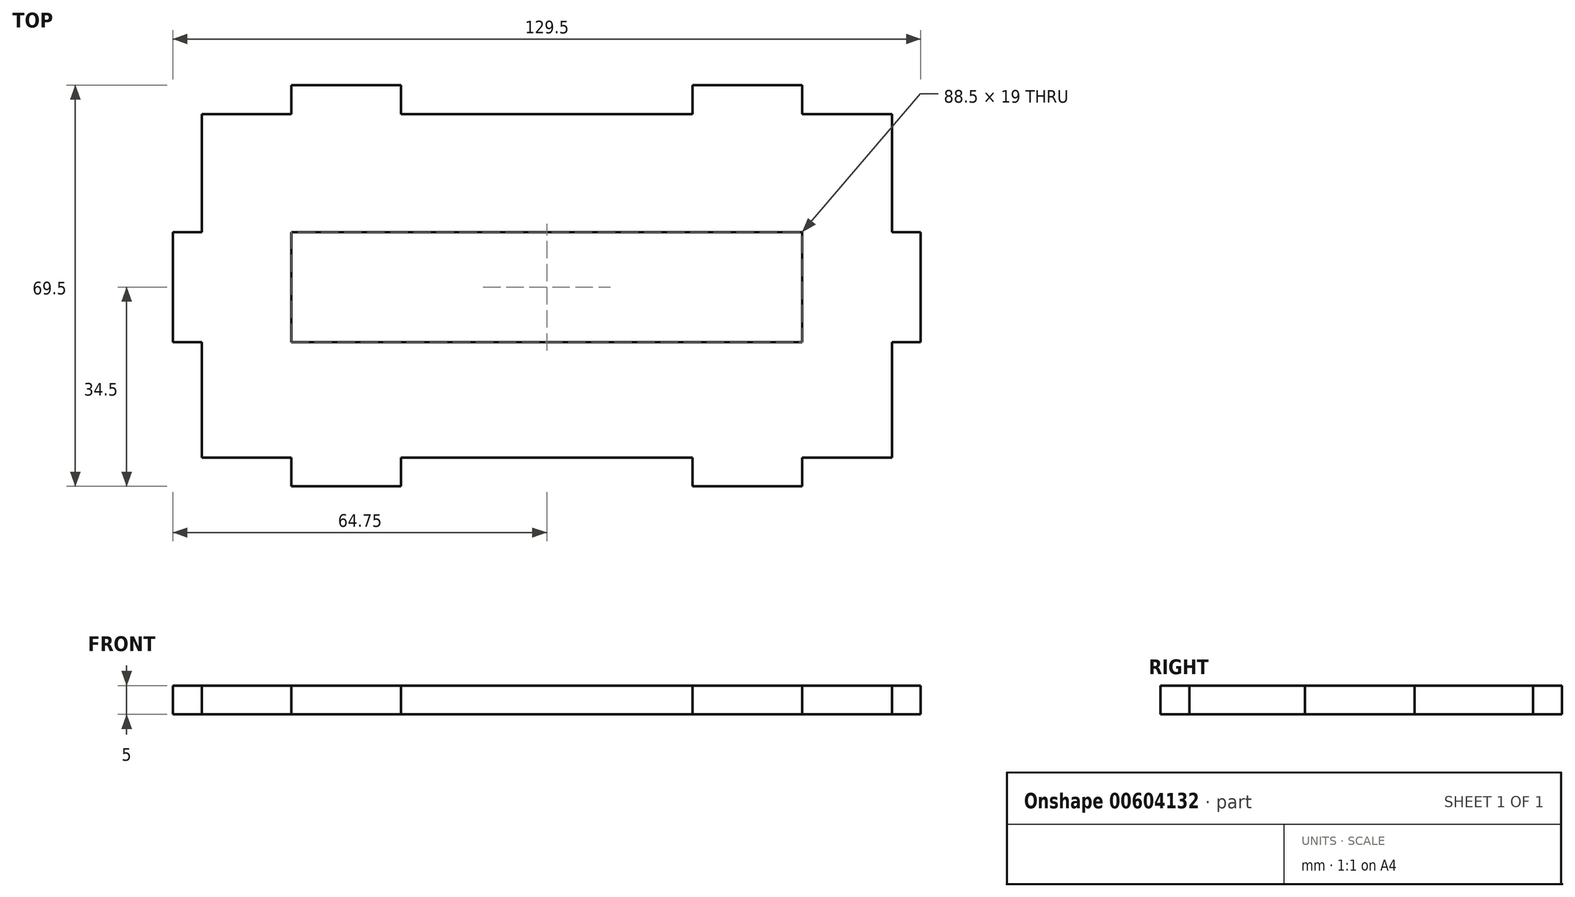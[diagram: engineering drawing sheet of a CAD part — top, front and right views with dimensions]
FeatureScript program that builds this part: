
annotation { "Feature Type Name" : "Feature", "Feature Type Description" : "" }
export const myFeature = defineFeature(function(context is Context, id is Id, definition is map)
    precondition{}
    {
        {
            var Q0;
            Q0=qCreatedBy(makeId("Top.planeOp"),FACE);
            var sketch = newSketch(context, id + "F0", { "sketchPlane" : qUnion([Q0])});
            skLineSegment(sketch, "E0.bottom", {"start": v(20.5, 0) * mm, "end": v(39.5, 0) * mm});
            skLineSegment(sketch, "E0.top", {"start": v(20.5, 69.5) * mm, "end": v(39.5, 69.5) * mm});
            skLineSegment(sketch, "E0.right", {"start": v(129.5, 25) * mm, "end": v(129.5, 44) * mm});
            skLineSegment(sketch, "E1.bottom", {"start": v(5, 64.5) * mm, "end": v(20.5, 64.5) * mm});
            skLineSegment(sketch, "E1.top", {"start": v(5, 5) * mm, "end": v(20.5, 5) * mm});
            skLineSegment(sketch, "E1.left", {"start": v(5, 64.5) * mm, "end": v(5, 44) * mm});
            skLineSegment(sketch, "E1.right", {"start": v(124.5, 64.5) * mm, "end": v(124.5, 44) * mm});
            skLineSegment(sketch, "E2.left", {"start": v(20.5, 69.5) * mm, "end": v(20.5, 64.5) * mm});
            skLineSegment(sketch, "E2.right", {"start": v(39.5, 69.5) * mm, "end": v(39.5, 64.5) * mm});
            skLineSegment(sketch, "E3.bottom", {"start": v(90, 0) * mm, "end": v(109, 0) * mm});
            skLineSegment(sketch, "E3.top", {"start": v(90, 69.5) * mm, "end": v(109, 69.5) * mm});
            skLineSegment(sketch, "E3.left", {"start": v(90, 0) * mm, "end": v(90, 5) * mm});
            skLineSegment(sketch, "E3.right", {"start": v(109, 0) * mm, "end": v(109, 5) * mm});
            skLineSegment(sketch, "E4.left", {"start": v(0, 35) * mm, "end": v(0, 25) * mm});
            skLineSegment(sketch, "E4.right", {"start": v(129.5, 34.75) * mm, "end": v(129.5, 25) * mm});
            skLineSegment(sketch, "E5.trimOffspring", {"start": v(0, 25) * mm, "end": v(0, 44) * mm});
            skLineSegment(sketch, "E6.bottom", {"start": v(0, 44) * mm, "end": v(5, 44) * mm});
            skLineSegment(sketch, "E6.top", {"start": v(0, 25) * mm, "end": v(5, 25) * mm});
            skLineSegment(sketch, "E6.left", {"start": v(0, 44) * mm, "end": v(0, 25) * mm});
            skLineSegment(sketch, "E6.right", {"start": v(129.5, 44) * mm, "end": v(129.5, 25) * mm});
            skLineSegment(sketch, "E7.trimOffspring", {"start": v(20.5, 5) * mm, "end": v(20.5, 0) * mm});
            skPoint(sketch, "E8.orphan", {"position": v(0, 69.5) * mm});
            skPoint(sketch, "E9.orphan", {"position": v(129.5, 69.5) * mm});
            skLineSegment(sketch, "E10.trimOffspring", {"start": v(109, 64.5) * mm, "end": v(109, 69.5) * mm});
            skLineSegment(sketch, "E11.trimOffspring", {"start": v(109, 64.5) * mm, "end": v(124.5, 64.5) * mm});
            skLineSegment(sketch, "E12.trimOffspring", {"start": v(90, 64.5) * mm, "end": v(90, 69.5) * mm});
            skLineSegment(sketch, "E13.trimOffspring", {"start": v(39.5, 5) * mm, "end": v(39.5, 0) * mm});
            skLineSegment(sketch, "E14.trimOffspring", {"start": v(39.5, 64.5) * mm, "end": v(90, 64.5) * mm});
            skLineSegment(sketch, "E15.trimOffspring", {"start": v(124.5, 44) * mm, "end": v(129.5, 44) * mm});
            skLineSegment(sketch, "E16.trimOffspring", {"start": v(124.5, 25) * mm, "end": v(129.5, 25) * mm});
            skLineSegment(sketch, "E17.trimOffspring", {"start": v(124.5, 25) * mm, "end": v(124.5, 5) * mm});
            skPoint(sketch, "E18.orphan", {"position": v(0, 18.5) * mm});
            skLineSegment(sketch, "E19.trimOffspring", {"start": v(0, 25) * mm, "end": v(0, 35) * mm});
            skLineSegment(sketch, "E20.trimOffspring", {"start": v(5, 25) * mm, "end": v(5, 5) * mm});
            skLineSegment(sketch, "E21.trimOffspring", {"start": v(39.5, 5) * mm, "end": v(90, 5) * mm});
            skPoint(sketch, "E22.orphan", {"position": v(129.5, 0) * mm});
            skPoint(sketch, "E23.orphan", {"position": v(129.5, 15.25) * mm});
            skLineSegment(sketch, "E24.bottom", {"start": v(20.5, 44) * mm, "end": v(109, 44) * mm});
            skLineSegment(sketch, "E24.top", {"start": v(20.5, 25) * mm, "end": v(109, 25) * mm});
            skLineSegment(sketch, "E24.left", {"start": v(20.5, 44) * mm, "end": v(20.5, 25) * mm});
            skLineSegment(sketch, "E24.right", {"start": v(109, 44) * mm, "end": v(109, 25) * mm});
            skLineSegment(sketch, "E25.trimOffspring", {"start": v(109, 5) * mm, "end": v(124.5, 5) * mm});
            skSolve(sketch);
        }
        {
            var Q0;
            Q0 = qSketchRegion(id + "F0", true);
            extrude(context, id + "F1", {"entities" : qUnion([Q0]), "depth" : 5 * mm, "offsetDistance" : 25.4 * mm});
        }
    });
